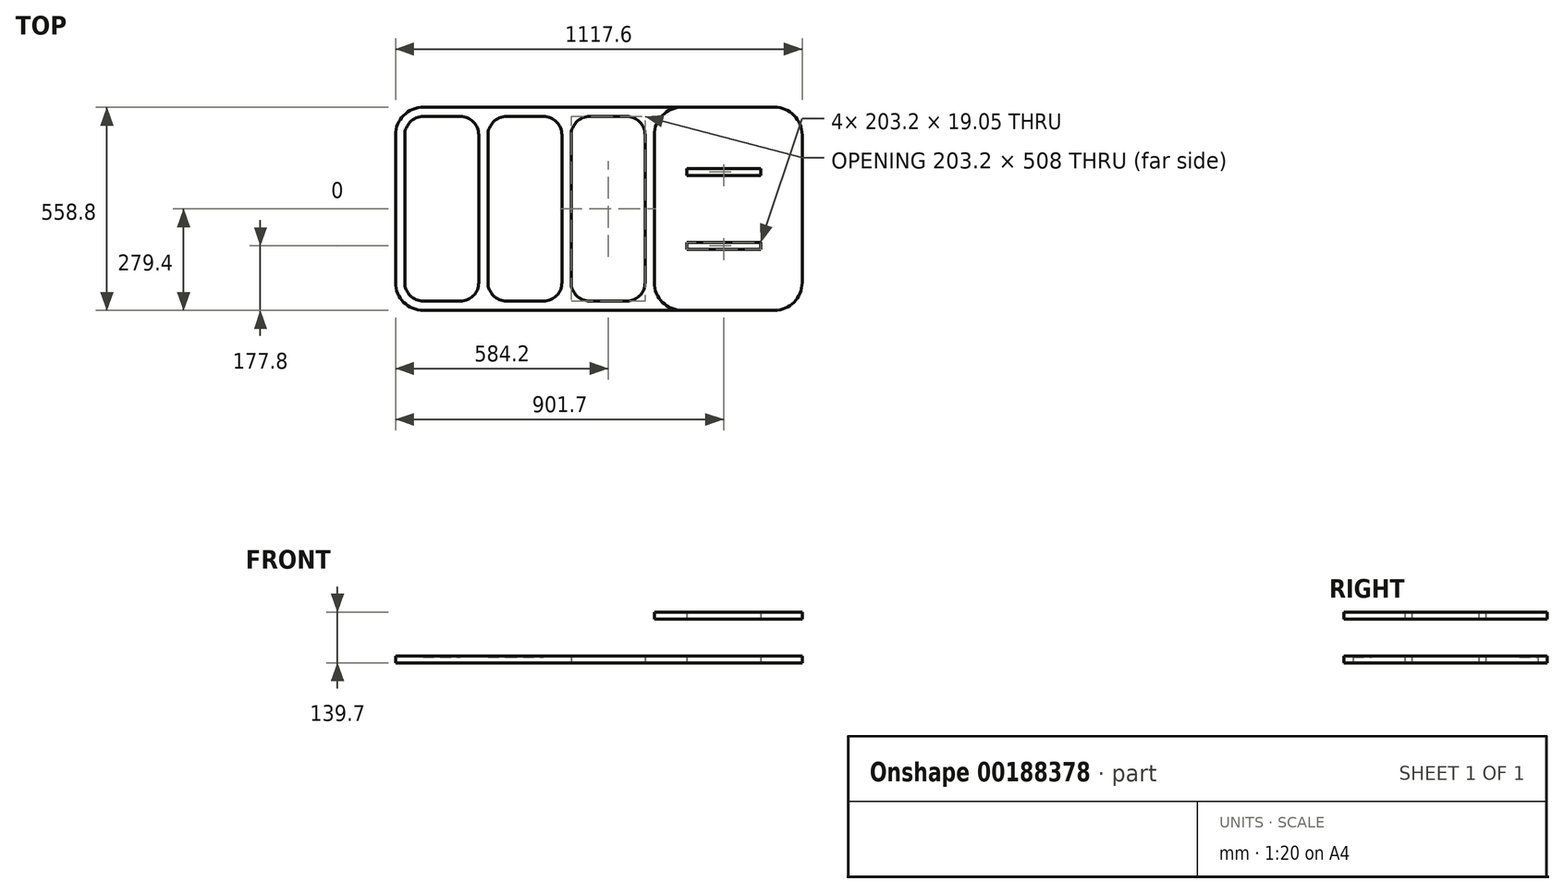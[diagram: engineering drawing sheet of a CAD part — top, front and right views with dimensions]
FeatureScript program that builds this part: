
annotation { "Feature Type Name" : "Feature", "Feature Type Description" : "" }
export const myFeature = defineFeature(function(context is Context, id is Id, definition is map)
    precondition{}
    {
        {
            var Q0;
            Q0=qCreatedBy(makeId("Top.planeOp"),FACE);
            var sketch = newSketch(context, id + "F0", { "sketchPlane" : qUnion([Q0])});
            skLineSegment(sketch, "E0.bottom", {"start": v(482.6, -279.4) * mm, "end": v(-482.6, -279.4) * mm});
            skLineSegment(sketch, "E0.top", {"start": v(482.6, 279.4) * mm, "end": v(-482.6, 279.4) * mm});
            skLineSegment(sketch, "E0.left", {"start": v(558.8, -203.2) * mm, "end": v(558.8, 203.2) * mm});
            skLineSegment(sketch, "E0.right", {"start": v(-558.8, -203.2) * mm, "end": v(-558.8, 203.2) * mm});
            skPoint(sketch, "E0.middle", {"position": v(0, 0) * mm});
            skPoint(sketch, "E1.visualSharp", {"position": v(-558.8, 279.4) * mm});
            skArc(sketch, "E1.filletArc", {"start": v(-482.6, 279.4) * mm, "mid": v(-536.48, 257.08) * mm, "end": v(-558.8, 203.2) * mm});
            skPoint(sketch, "E2.visualSharp", {"position": v(-558.8, -279.4) * mm});
            skArc(sketch, "E2.filletArc", {"start": v(-558.8, -203.2) * mm, "mid": v(-536.48, -257.08) * mm, "end": v(-482.6, -279.4) * mm});
            skPoint(sketch, "E3.visualSharp", {"position": v(558.8, -279.4) * mm});
            skArc(sketch, "E3.filletArc", {"start": v(482.6, -279.4) * mm, "mid": v(536.48, -257.08) * mm, "end": v(558.8, -203.2) * mm});
            skPoint(sketch, "E4.visualSharp", {"position": v(558.8, 279.4) * mm});
            skArc(sketch, "E4.filletArc", {"start": v(558.8, 203.2) * mm, "mid": v(536.48, 257.08) * mm, "end": v(482.6, 279.4) * mm});
            skArc(sketch, "E5.0", {"start": v(-482.6, 254) * mm, "mid": v(-518.52, 239.12) * mm, "end": v(-533.4, 203.2) * mm});
            skLineSegment(sketch, "E6.0", {"start": v(-533.4, -203.2) * mm, "end": v(-533.4, 203.2) * mm});
            skArc(sketch, "E7.0", {"start": v(-533.4, -203.2) * mm, "mid": v(-518.52, -239.12) * mm, "end": v(-482.6, -254) * mm});
            skLineSegment(sketch, "E8", {"start": v(558.8, 203.2) * mm, "end": v(558.8, 453.78) * mm, "construction": true});
            skLineSegment(sketch, "E9", {"start": v(558.8, 453.78) * mm, "end": v(152.4, 453.78) * mm, "construction": true});
            skLineSegment(sketch, "E10", {"start": v(152.4, 453.78) * mm, "end": v(152.4, -279.4) * mm, "construction": true});
            skLineSegment(sketch, "E11", {"start": v(-533.4, 0) * mm, "end": v(127, 0) * mm, "construction": true});
            skLineSegment(sketch, "E12", {"start": v(-203.2, 0) * mm, "end": v(-203.2, -134.6) * mm, "construction": true});
            skArc(sketch, "E13.MirrorCS", {"start": v(76.2, 254) * mm, "mid": v(112.12, 239.12) * mm, "end": v(127, 203.2) * mm});
            skArc(sketch, "E14.MirrorCS", {"start": v(127, -203.2) * mm, "mid": v(112.12, -239.12) * mm, "end": v(76.2, -254) * mm});
            skLineSegment(sketch, "E15", {"start": v(-482.6, 254) * mm, "end": v(-381, 254) * mm});
            skLineSegment(sketch, "E16", {"start": v(-482.6, -254) * mm, "end": v(-381, -254) * mm});
            skLineSegment(sketch, "E17.trimOffspring", {"start": v(127, 203.2) * mm, "end": v(127, 0) * mm});
            skLineSegment(sketch, "E18", {"start": v(127, 0) * mm, "end": v(127, -203.2) * mm});
            skLineSegment(sketch, "E19", {"start": v(127, -101.6) * mm, "end": v(558.8, -101.6) * mm, "construction": true});
            skLineSegment(sketch, "E20.MirrorCS", {"start": v(127, -92.08) * mm, "end": v(558.8, -92.08) * mm, "construction": true});
            skLineSegment(sketch, "E21.MirrorCS", {"start": v(127, -111.13) * mm, "end": v(558.8, -111.13) * mm, "construction": true});
            skLineSegment(sketch, "E22", {"start": v(342.9, 111.12) * mm, "end": v(342.9, 92.07) * mm, "construction": true});
            skLineSegment(sketch, "E23.0", {"start": v(241.3, 111.12) * mm, "end": v(241.3, 92.07) * mm, "construction": true});
            skLineSegment(sketch, "E24.MirrorCS", {"start": v(444.5, 111.12) * mm, "end": v(444.5, 92.07) * mm, "construction": true});
            skLineSegment(sketch, "E25.bottom", {"start": v(241.3, 111.12) * mm, "end": v(444.5, 111.12) * mm});
            skLineSegment(sketch, "E25.top", {"start": v(241.3, 92.07) * mm, "end": v(444.5, 92.07) * mm});
            skLineSegment(sketch, "E25.left", {"start": v(241.3, 111.12) * mm, "end": v(241.3, 92.07) * mm});
            skLineSegment(sketch, "E25.right", {"start": v(444.5, 111.12) * mm, "end": v(444.5, 92.07) * mm});
            skLineSegment(sketch, "E26.MirrorCS", {"start": v(241.3, -92.08) * mm, "end": v(444.5, -92.08) * mm});
            skLineSegment(sketch, "E27.MirrorCS", {"start": v(444.5, -111.13) * mm, "end": v(444.5, -92.08) * mm});
            skLineSegment(sketch, "E28.MirrorCS", {"start": v(241.3, -111.13) * mm, "end": v(444.5, -111.13) * mm});
            skLineSegment(sketch, "E29.MirrorCS", {"start": v(241.3, -111.13) * mm, "end": v(241.3, -92.08) * mm});
            skLineSegment(sketch, "E30", {"start": v(482.6, -279.4) * mm, "end": v(482.6, 279.4) * mm, "construction": true});
            skLineSegment(sketch, "E31", {"start": v(-482.6, 203.2) * mm, "end": v(482.6, 203.2) * mm, "construction": true});
            skLineSegment(sketch, "E32.MirrorCS", {"start": v(-482.6, -203.2) * mm, "end": v(482.6, -203.2) * mm, "construction": true});
            skLineSegment(sketch, "E33", {"start": v(0, -279.4) * mm, "end": v(0, 0) * mm, "construction": true});
            skLineSegment(sketch, "E34.0", {"start": v(-304.8, 203.2) * mm, "end": v(-304.8, -203.2) * mm});
            skLineSegment(sketch, "E35.MirrorCS", {"start": v(-101.6, 203.2) * mm, "end": v(-101.6, -203.2) * mm});
            skPoint(sketch, "E36.orphan", {"position": v(-304.8, 0) * mm});
            skPoint(sketch, "E37.orphan", {"position": v(-304.8, -134.6) * mm});
            skPoint(sketch, "E38.orphan", {"position": v(-101.6, 0) * mm});
            skPoint(sketch, "E39.orphan", {"position": v(-101.6, -134.6) * mm});
            skLineSegment(sketch, "E40.0", {"start": v(-330.2, 203.2) * mm, "end": v(-330.2, -203.2) * mm});
            skLineSegment(sketch, "E41.0", {"start": v(-76.2, 203.2) * mm, "end": v(-76.2, -203.2) * mm});
            skArc(sketch, "E42.filletArc", {"start": v(-330.2, 203.2) * mm, "mid": v(-345.08, 239.12) * mm, "end": v(-381, 254) * mm});
            skLineSegment(sketch, "E43", {"start": v(-254, 254) * mm, "end": v(-152.4, 254) * mm});
            skLineSegment(sketch, "E44", {"start": v(-25.4, 254) * mm, "end": v(76.2, 254) * mm});
            skPoint(sketch, "E45.visualSharp", {"position": v(-304.8, 254) * mm});
            skArc(sketch, "E45.filletArc", {"start": v(-254, 254) * mm, "mid": v(-289.92, 239.12) * mm, "end": v(-304.8, 203.2) * mm});
            skPoint(sketch, "E46.visualSharp", {"position": v(-101.6, 254) * mm});
            skArc(sketch, "E46.filletArc", {"start": v(-101.6, 203.2) * mm, "mid": v(-116.48, 239.12) * mm, "end": v(-152.4, 254) * mm});
            skPoint(sketch, "E47.visualSharp", {"position": v(-76.2, 254) * mm});
            skArc(sketch, "E47.filletArc", {"start": v(-25.4, 254) * mm, "mid": v(-61.32, 239.12) * mm, "end": v(-76.2, 203.2) * mm});
            skArc(sketch, "E48.filletArc", {"start": v(-381, -254) * mm, "mid": v(-345.08, -239.12) * mm, "end": v(-330.2, -203.2) * mm});
            skLineSegment(sketch, "E49.MirrorCS", {"start": v(-254, -254) * mm, "end": v(-152.4, -254) * mm});
            skArc(sketch, "E50.MirrorCS", {"start": v(-101.6, -203.2) * mm, "mid": v(-116.48, -239.12) * mm, "end": v(-152.4, -254) * mm});
            skArc(sketch, "E51.MirrorCS", {"start": v(-254, -254) * mm, "mid": v(-289.92, -239.12) * mm, "end": v(-304.8, -203.2) * mm});
            skArc(sketch, "E52.MirrorCS", {"start": v(-25.4, -254) * mm, "mid": v(-61.32, -239.12) * mm, "end": v(-76.2, -203.2) * mm});
            skLineSegment(sketch, "E53.MirrorCS", {"start": v(-25.4, -254) * mm, "end": v(76.2, -254) * mm});
            skSolve(sketch);
        }
        {
            var Q0;
            Q0=makeQuery(id+"F0.imprint","IMPRINT",FACE,{"disambiguationData":[TD([[makeQuery(id+"F0.imprint","IMPRINT",EDGE,{"derivedFrom":sQuery(id+"F0.wireOp",EDGE,"E0.bottom")}),-1.0]])]});
            extrude(context, id + "F1", {"entities" : qUnion([Q0]), "depth" : 19.05 * mm});
        }
        {
            var Q0;
            Q0=makeQuery(id+"F0.imprint","IMPRINT",FACE,{"disambiguationData":[TD([[makeQuery(id+"F0.imprint","IMPRINT",EDGE,{"derivedFrom":sQuery(id+"F0.wireOp",EDGE,"E5.0")}),1.0]])]});
            var Q1;
            Q1=makeQuery(id+"F0.imprint","IMPRINT",FACE,{"disambiguationData":[TD([[makeQuery(id+"F0.imprint","IMPRINT",EDGE,{"derivedFrom":sQuery(id+"F0.wireOp",EDGE,"E34.0")}),1.0]])]});
            var Q2;
            Q2=makeQuery(id+"F0.imprint","IMPRINT",FACE,{"disambiguationData":[TD([[makeQuery(id+"F0.imprint","IMPRINT",EDGE,{"derivedFrom":sQuery(id+"F0.wireOp",EDGE,"E13.MirrorCS")}),-1.0]])]});
            extrude(context, id + "F2", {"entities" : qUnion([Q0, Q1, Q2]), "operationType" : NewBodyOperationType.ADD, "depth" : 15.88 * mm});
        }
        {
            var Q0;
            Q0=makeQuery(id+"F1.opExtrude","CAP_FACE",FACE,{"disambiguationData":[OSD([sQuery(id+"F0.wireOp",EDGE,"E0.bottom"),sQuery(id+"F0.wireOp",EDGE,"E0.top"),sQuery(id+"F0.wireOp",EDGE,"E0.left"),sQuery(id+"F0.wireOp",EDGE,"E0.right"),sQuery(id+"F0.wireOp",EDGE,"E1.filletArc"),sQuery(id+"F0.wireOp",EDGE,"E2.filletArc"),sQuery(id+"F0.wireOp",EDGE,"E3.filletArc"),sQuery(id+"F0.wireOp",EDGE,"E4.filletArc"),sQuery(id+"F0.wireOp",EDGE,"E5.0"),sQuery(id+"F0.wireOp",EDGE,"E6.0"),sQuery(id+"F0.wireOp",EDGE,"E7.0"),sQuery(id+"F0.wireOp",EDGE,"E13.MirrorCS"),sQuery(id+"F0.wireOp",EDGE,"E14.MirrorCS"),sQuery(id+"F0.wireOp",EDGE,"E15"),sQuery(id+"F0.wireOp",EDGE,"E16"),sQuery(id+"F0.wireOp",EDGE,"E17.trimOffspring")])],"isStart":false});
            cPlane(context, id + "F3", {"entities" : qUnion([Q0]), "cplaneType" : CPlaneType.OFFSET, "offset" : 101.6 * mm, "width" : 152.4 * mm, "height" : 152.4 * mm});
        }
        {
            var Q0;
            Q0=qCreatedBy(id+"F3.planeOp",FACE);
            var sketch = newSketch(context, id + "F4", { "sketchPlane" : qUnion([Q0])});
            skLineSegment(sketch, "E54.0", {"start": v(558.8, -203.2) * mm, "end": v(558.8, 203.2) * mm});
            skArc(sketch, "E55.0", {"start": v(558.8, 203.2) * mm, "mid": v(536.48, 257.08) * mm, "end": v(482.6, 279.4) * mm});
            skArc(sketch, "E56.0", {"start": v(482.6, -279.4) * mm, "mid": v(536.48, -257.08) * mm, "end": v(558.8, -203.2) * mm});
            skLineSegment(sketch, "E57", {"start": v(558.8, 0) * mm, "end": v(152.4, 0) * mm, "construction": true});
            skPoint(sketch, "E57.endSnap0", {"position": v(558.8, 0) * mm});
            skLineSegment(sketch, "E58", {"start": v(355.6, 0) * mm, "end": v(355.6, 87.95) * mm, "construction": true});
            skArc(sketch, "E59.MirrorCS", {"start": v(152.4, 203.2) * mm, "mid": v(174.72, 257.08) * mm, "end": v(228.6, 279.4) * mm});
            skLineSegment(sketch, "E60.MirrorCS", {"start": v(152.4, -203.2) * mm, "end": v(152.4, 203.2) * mm});
            skArc(sketch, "E61.MirrorCS", {"start": v(228.6, -279.4) * mm, "mid": v(174.72, -257.08) * mm, "end": v(152.4, -203.2) * mm});
            skLineSegment(sketch, "E62", {"start": v(228.6, 279.4) * mm, "end": v(482.6, 279.4) * mm});
            skLineSegment(sketch, "E63", {"start": v(228.6, -279.4) * mm, "end": v(482.6, -279.4) * mm});
            skLineSegment(sketch, "E64.0", {"start": v(241.3, 111.12) * mm, "end": v(444.5, 111.12) * mm});
            skLineSegment(sketch, "E65.0", {"start": v(241.3, 111.12) * mm, "end": v(241.3, 92.07) * mm});
            skLineSegment(sketch, "E66.0", {"start": v(444.5, 111.12) * mm, "end": v(444.5, 92.07) * mm});
            skLineSegment(sketch, "E67.0", {"start": v(241.3, 92.07) * mm, "end": v(444.5, 92.07) * mm});
            skLineSegment(sketch, "E68.0", {"start": v(241.3, -92.08) * mm, "end": v(444.5, -92.08) * mm});
            skLineSegment(sketch, "E69.0", {"start": v(444.5, -111.13) * mm, "end": v(444.5, -92.08) * mm});
            skLineSegment(sketch, "E70.0", {"start": v(241.3, -111.13) * mm, "end": v(444.5, -111.13) * mm});
            skLineSegment(sketch, "E71.0", {"start": v(241.3, -111.13) * mm, "end": v(241.3, -92.08) * mm});
            skSolve(sketch);
        }
        {
            var Q0;
            Q0 = qSketchRegion(id + "F4", true);
            extrude(context, id + "F5", {"entities" : qUnion([Q0]), "depth" : 19.05 * mm});
        }
        {
            var Q0;
            Q0=makeQuery(id+"F0.imprint","IMPRINT",FACE,{"disambiguationData":[TD([[makeQuery(id+"F0.imprint","IMPRINT",EDGE,{"derivedFrom":sQuery(id+"F0.wireOp",EDGE,"E26.MirrorCS")}),-1.0]])]});
            var Q1;
            Q1=makeQuery(id+"F0.imprint","IMPRINT",FACE,{"disambiguationData":[TD([[makeQuery(id+"F0.imprint","IMPRINT",EDGE,{"derivedFrom":sQuery(id+"F0.wireOp",EDGE,"E25.bottom")}),-1.0]])]});
            extrude(context, id + "F6", {"entities" : qUnion([Q0, Q1]), "operationType" : NewBodyOperationType.REMOVE, "oppositeDirection" : true, "depth" : 25.4 * mm});
        }
        {
            var Q0;
            Q0=makeQuery(id+"F4.imprint","IMPRINT",FACE,{"disambiguationData":[TD([[makeQuery(id+"F4.imprint","IMPRINT",EDGE,{"derivedFrom":sQuery(id+"F4.wireOp",EDGE,"E64.0")}),-1.0]])]});
            var Q1;
            Q1=makeQuery(id+"F4.imprint","IMPRINT",FACE,{"disambiguationData":[TD([[makeQuery(id+"F4.imprint","IMPRINT",EDGE,{"derivedFrom":sQuery(id+"F4.wireOp",EDGE,"E68.0")}),-1.0]])]});
            extrude(context, id + "F7", {"entities" : qUnion([Q0, Q1]), "operationType" : NewBodyOperationType.REMOVE, "oppositeDirection" : true, "depth" : 25.4 * mm});
        }
    });
